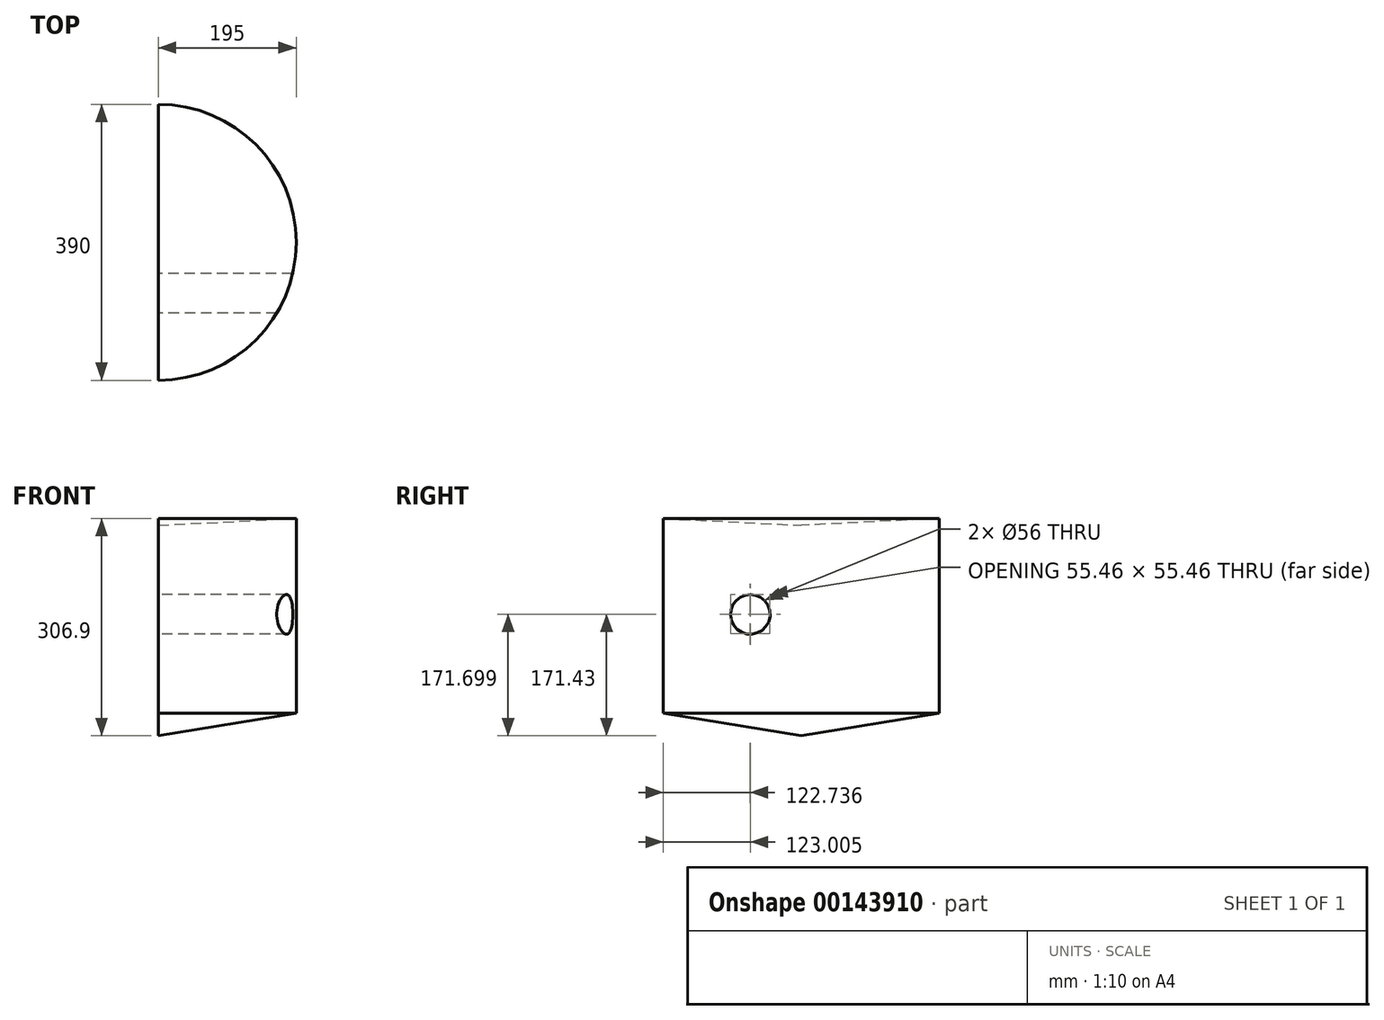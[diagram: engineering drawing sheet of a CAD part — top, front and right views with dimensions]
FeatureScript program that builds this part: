
annotation { "Feature Type Name" : "Feature", "Feature Type Description" : "" }
export const myFeature = defineFeature(function(context is Context, id is Id, definition is map)
    precondition{}
    {
        {
            var Q0;
            Q0=qCreatedBy(makeId("Right.planeOp"),FACE);
            var sketch = newSketch(context, id + "F0", { "sketchPlane" : qUnion([Q0])});
            skLineSegment(sketch, "E0", {"start": v(-195, 135.47) * mm, "end": v(-195, -139.43) * mm});
            skLineSegment(sketch, "E1", {"start": v(0, 0) * mm, "end": v(0, 125.7) * mm});
            skLineSegment(sketch, "E2", {"start": v(-100, 120.62) * mm, "end": v(-100, -90.18) * mm});
            skLineSegment(sketch, "E3", {"start": v(-195, 135.47) * mm, "end": v(0, 125.7) * mm});
            skLineSegment(sketch, "E4", {"start": v(-195, -139.43) * mm, "end": v(0, -171.43) * mm});
            skLineSegment(sketch, "E5", {"start": v(0, -171.43) * mm, "end": v(0, 0) * mm});
            skLineSegment(sketch, "E6", {"start": v(-100, -90.18) * mm, "end": v(0, -92.73) * mm});
            skSolve(sketch);
        }
        {
            var Q0;
            {var subQ1=sQuery(id+"F0.wireOp",EDGE,"E1");Q0=makeQuery(id+"F0.imprint","IMPRINT",FACE,{"disambiguationData":[TD([[makeQuery(id+"F0.imprint","IMPRINT",EDGE,{"derivedFrom":subQ1}),1.0]])]});}
            var Q1;
            Q1=sQuery(id+"F0.wireOp",EDGE,"E0");
            var Q2;
            Q2=sQuery(id+"F0.wireOp",EDGE,"E1");
            revolve(context, id + "F1", {"entities" : qUnion([Q0]), "surfaceEntities" : qUnion([Q1]), "axis" : qUnion([Q2]), "revolveType" : RevolveType.ONE_DIRECTION, "angle" : 180 * degree});
        }
        {
            var Q0;
            Q0=makeQuery(id+"F0.imprint","IMPRINT",FACE,{"disambiguationData":[TD([[makeQuery(id+"F0.imprint","IMPRINT",EDGE,{"derivedFrom":sQuery(id+"F0.wireOp",EDGE,"E0")}),1.0]])]});
            var Q1;
            Q1=sQuery(id+"F0.wireOp",EDGE,"E2");
            var Q2;
            Q2=sQuery(id+"F0.wireOp",EDGE,"E1");
            revolve(context, id + "F2", {"entities" : qUnion([Q0]), "surfaceEntities" : qUnion([Q1]), "axis" : qUnion([Q2]), "revolveType" : RevolveType.ONE_DIRECTION, "angle" : 180 * degree});
        }
        {
            var Q0;
            Q0=qCreatedBy(makeId("Right.planeOp"),FACE);
            var sketch = newSketch(context, id + "F3", { "sketchPlane" : qUnion([Q0])});
            skCircle(sketch, "E7", {"center": v(-72, 0) * mm, "radius": 28 * mm});
            skLineSegment(sketch, "E8.0", {"start": v(-100, 120.62) * mm, "end": v(-100, -90.18) * mm, "construction": true});
            skSolve(sketch);
        }
        {
            var Q0;
            Q0=makeQuery(id+"F3.imprint","IMPRINT",FACE,{"disambiguationData":[TD([[makeQuery(id+"F3.imprint","IMPRINT",EDGE,{"derivedFrom":sQuery(id+"F3.wireOp",EDGE,"E7")}),1.0]])]});
            extrude(context, id + "F4", {"entities" : qUnion([Q0]), "endBound" : BoundingType.SYMMETRIC, "depth" : 500 * mm});
        }
        {
            var Q0;
            Q0=makeQuery(id+"F4.opExtrude","SWEPT_BODY",BODY,{"disambiguationData":[OSD([sQuery(id+"F3.wireOp",EDGE,"E7")])]});
            var Q1;
            Q1=makeQuery(id+"F2.opRevolve","SWEPT_BODY",BODY,{"disambiguationData":[OSD([sQuery(id+"F0.wireOp",EDGE,"E0"),sQuery(id+"F0.wireOp",EDGE,"E2"),sQuery(id+"F0.wireOp",EDGE,"E3"),sQuery(id+"F0.wireOp",EDGE,"E4"),sQuery(id+"F0.wireOp",EDGE,"E5"),sQuery(id+"F0.wireOp",EDGE,"emXCJjvb-PiEe-Rl0x-nJkn-ibfQYgi9xcq8"),sQuery(id+"F0.wireOp",EDGE,"E6")])]});
            booleanBodies(context, id + "F5", {"operationType" : BooleanOperationType.SUBTRACTION, "tools" : qUnion([Q0]), "targets" : qUnion([Q1]), "keepTools" : true});
        }
        {
            var Q0;
            Q0=makeQuery(id+"F4.opExtrude","SWEPT_BODY",BODY,{"disambiguationData":[OSD([sQuery(id+"F3.wireOp",EDGE,"E7")])]});
            var Q1;
            Q1=makeQuery(id+"F1.opRevolve","SWEPT_BODY",BODY,{"disambiguationData":[OSD([sQuery(id+"F0.wireOp",EDGE,"E1"),sQuery(id+"F0.wireOp",EDGE,"E2"),sQuery(id+"F0.wireOp",EDGE,"E5"),sQuery(id+"F0.wireOp",EDGE,"emXCJjvb-PiEe-Rl0x-nJkn-ibfQYgi9xcq8"),sQuery(id+"F0.wireOp",EDGE,"E6")])]});
            booleanBodies(context, id + "F6", {"operationType" : BooleanOperationType.SUBTRACTION, "tools" : qUnion([Q0]), "targets" : qUnion([Q1])});
        }
    });
